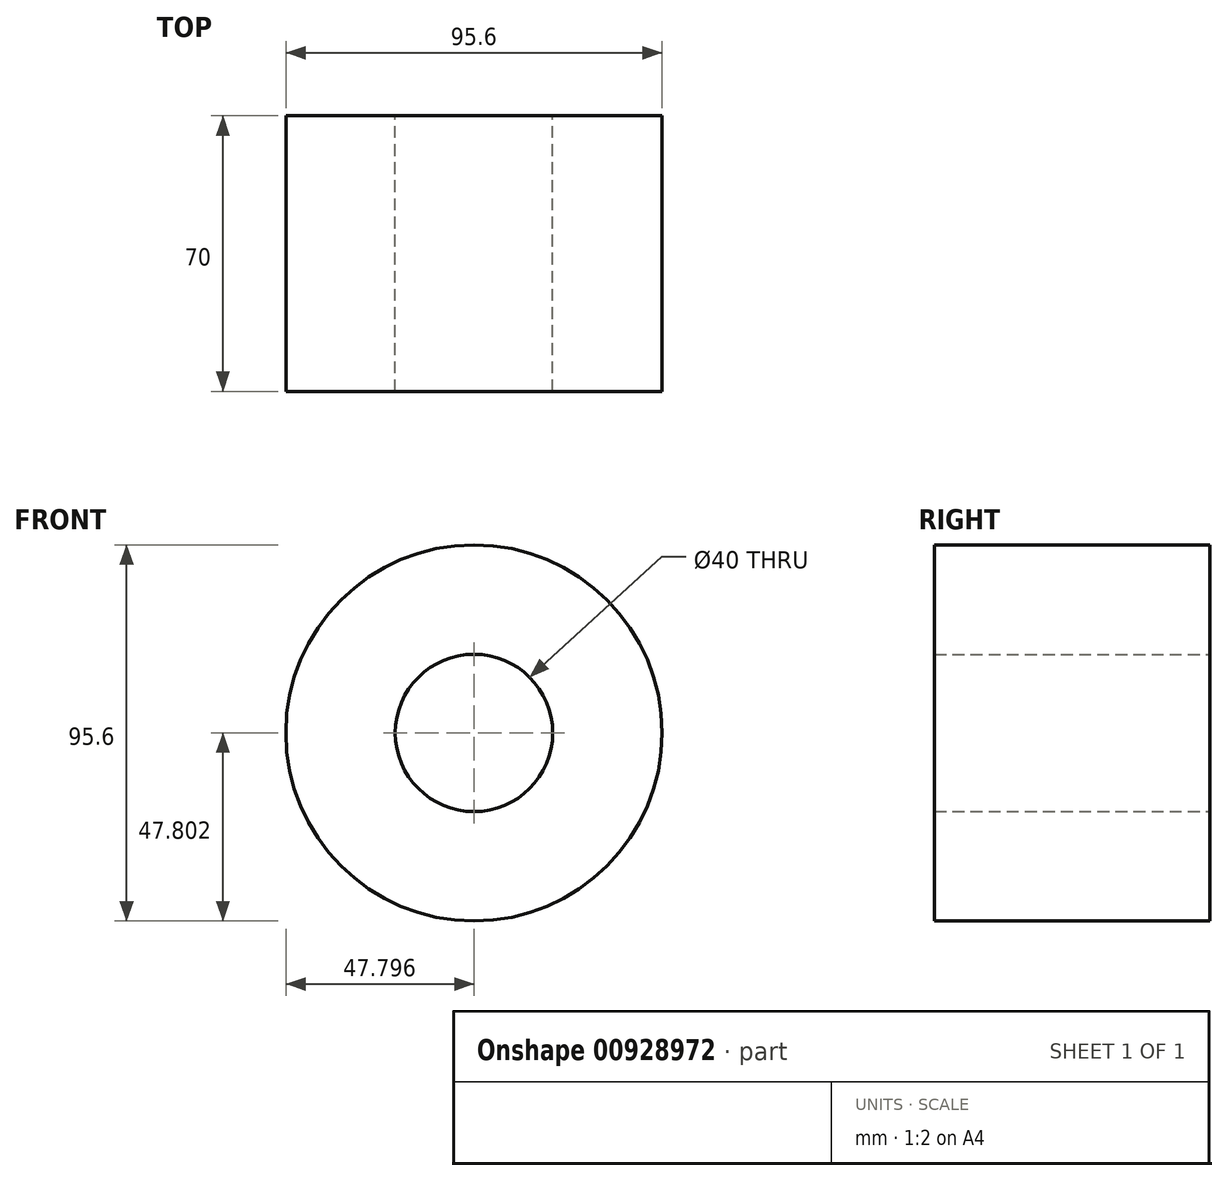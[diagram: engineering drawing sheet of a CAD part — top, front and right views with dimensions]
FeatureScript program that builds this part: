
annotation { "Feature Type Name" : "Feature", "Feature Type Description" : "" }
export const myFeature = defineFeature(function(context is Context, id is Id, definition is map)
    precondition{}
    {
        {
            var Q0;
            Q0=qCreatedBy(makeId("Front.planeOp"),FACE);
            var sketch = newSketch(context, id + "F0", { "sketchPlane" : qUnion([Q0])});
            skCircle(sketch, "E0", {"center": v(251.45, -96.2) * mm, "radius": 20 * mm});
            skCircle(sketch, "E1", {"center": v(251.45, -96.2) * mm, "radius": 47.8 * mm});
            skSolve(sketch);
        }
        {
            var Q0;
            Q0=makeQuery(id+"F0.imprint","IMPRINT",FACE,{"disambiguationData":[TD([[makeQuery(id+"F0.imprint","IMPRINT",EDGE,{"derivedFrom":sQuery(id+"F0.wireOp",EDGE,"E0")}),-1.0]])]});
            extrude(context, id + "F1", {"entities" : qUnion([Q0]), "depth" : 70 * mm, "offsetDistance" : 25 * mm});
        }
    });
